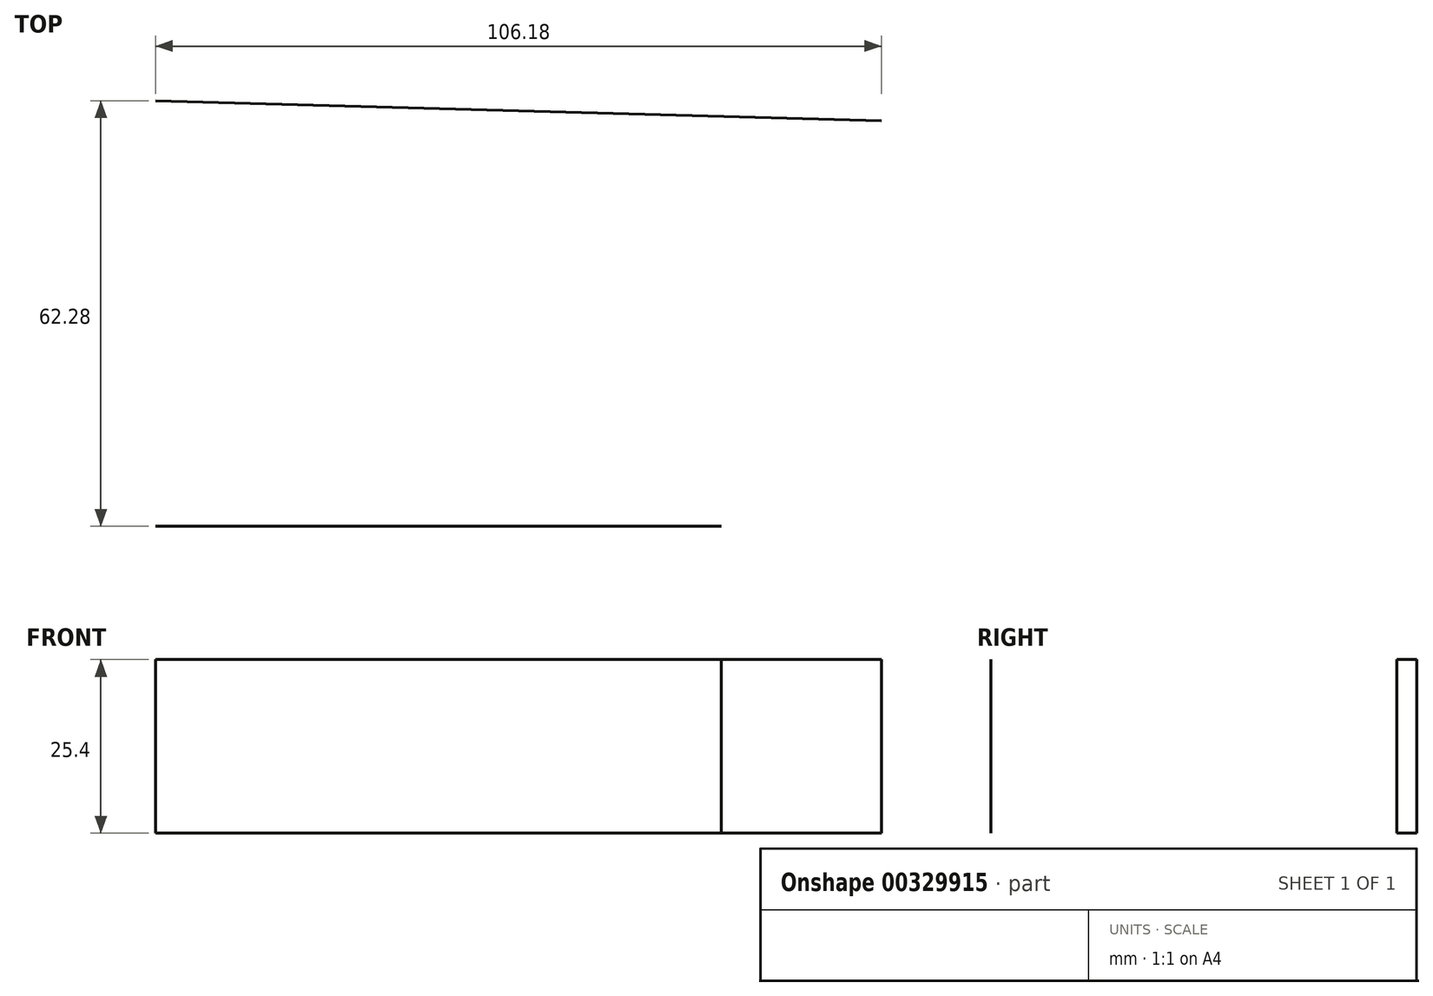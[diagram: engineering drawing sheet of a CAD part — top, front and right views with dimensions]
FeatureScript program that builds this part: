
annotation { "Feature Type Name" : "Feature", "Feature Type Description" : "" }
export const myFeature = defineFeature(function(context is Context, id is Id, definition is map)
    precondition{}
    {
        {
            var Q0;
            Q0=qCreatedBy(makeId("Top.planeOp"),FACE);
            var sketch = newSketch(context, id + "F0", { "sketchPlane" : qUnion([Q0])});
            skLineSegment(sketch, "E0", {"start": v(-40.46, -35.33) * mm, "end": v(42.29, -35.33) * mm});
            skSolve(sketch);
        }
        {
            var Q0;
            Q0=sQuery(id+"F0.wireOp",EDGE,"E0");
            extrude(context, id + "F1", {"bodyType" : ToolBodyType.SURFACE, "surfaceEntities" : qUnion([Q0]), "depth" : 25.4 * mm});
        }
        {
            var Q0;
            Q0=qCreatedBy(makeId("Top.planeOp"),FACE);
            var sketch = newSketch(context, id + "F2", { "sketchPlane" : qUnion([Q0])});
            skLineSegment(sketch, "E1", {"start": v(-40.46, 26.95) * mm, "end": v(65.72, 24.02) * mm});
            skSolve(sketch);
        }
        {
            var Q0;
            Q0 = qBodyType(qCreatedBy(id + "F2" ,EDGE), BodyType.WIRE);
            extrude(context, id + "F3", {"bodyType" : ToolBodyType.SURFACE, "surfaceEntities" : qUnion([Q0]), "depth" : 25.4 * mm});
        }
    });
